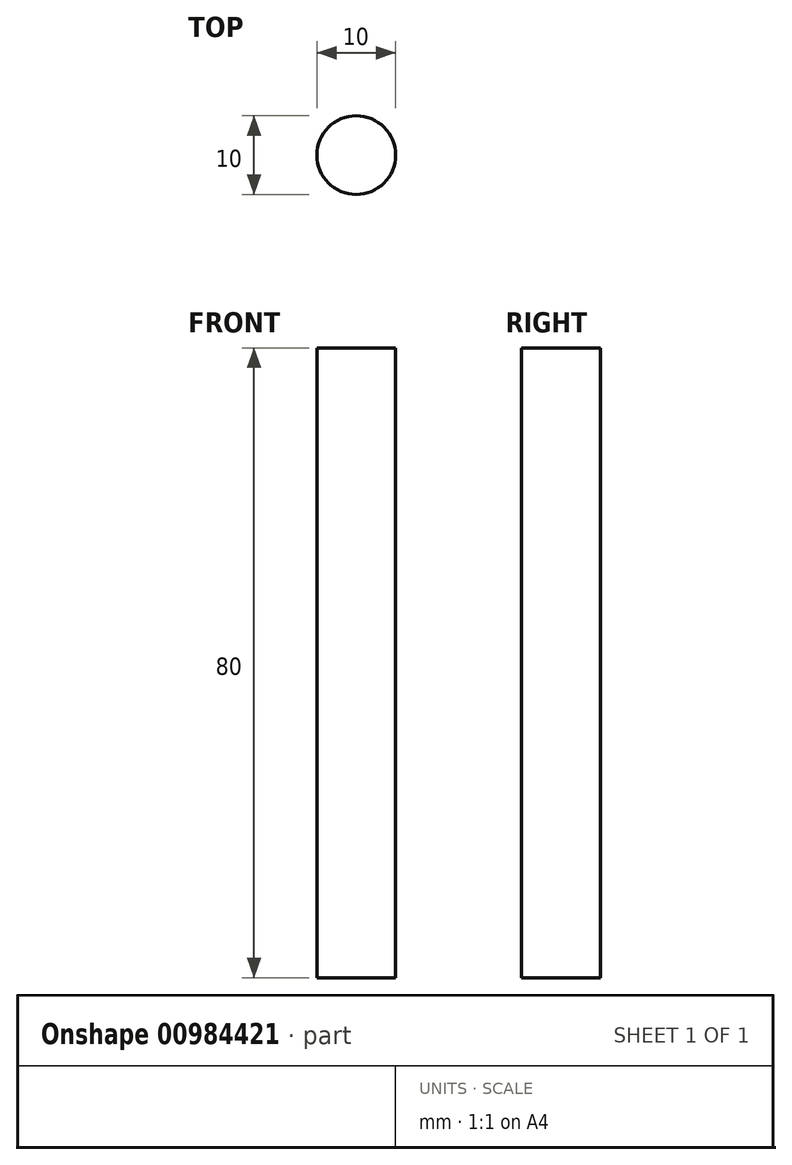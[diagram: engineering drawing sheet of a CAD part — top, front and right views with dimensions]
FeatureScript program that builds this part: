
annotation { "Feature Type Name" : "Feature", "Feature Type Description" : "" }
export const myFeature = defineFeature(function(context is Context, id is Id, definition is map)
    precondition{}
    {
        {
            var Q0;
            Q0=qCreatedBy(makeId("Top.planeOp"),FACE);
            var sketch = newSketch(context, id + "F0", { "sketchPlane" : qUnion([Q0])});
            skCircle(sketch, "E0", {"center": v(0, 0) * mm, "radius": 5 * mm});
            skSolve(sketch);
        }
        {
            var Q0;
            Q0 = qSketchRegion(id + "F0", true);
            extrude(context, id + "F1", {"entities" : qUnion([Q0]), "depth" : 80 * mm, "offsetDistance" : 25 * mm});
        }
    });
